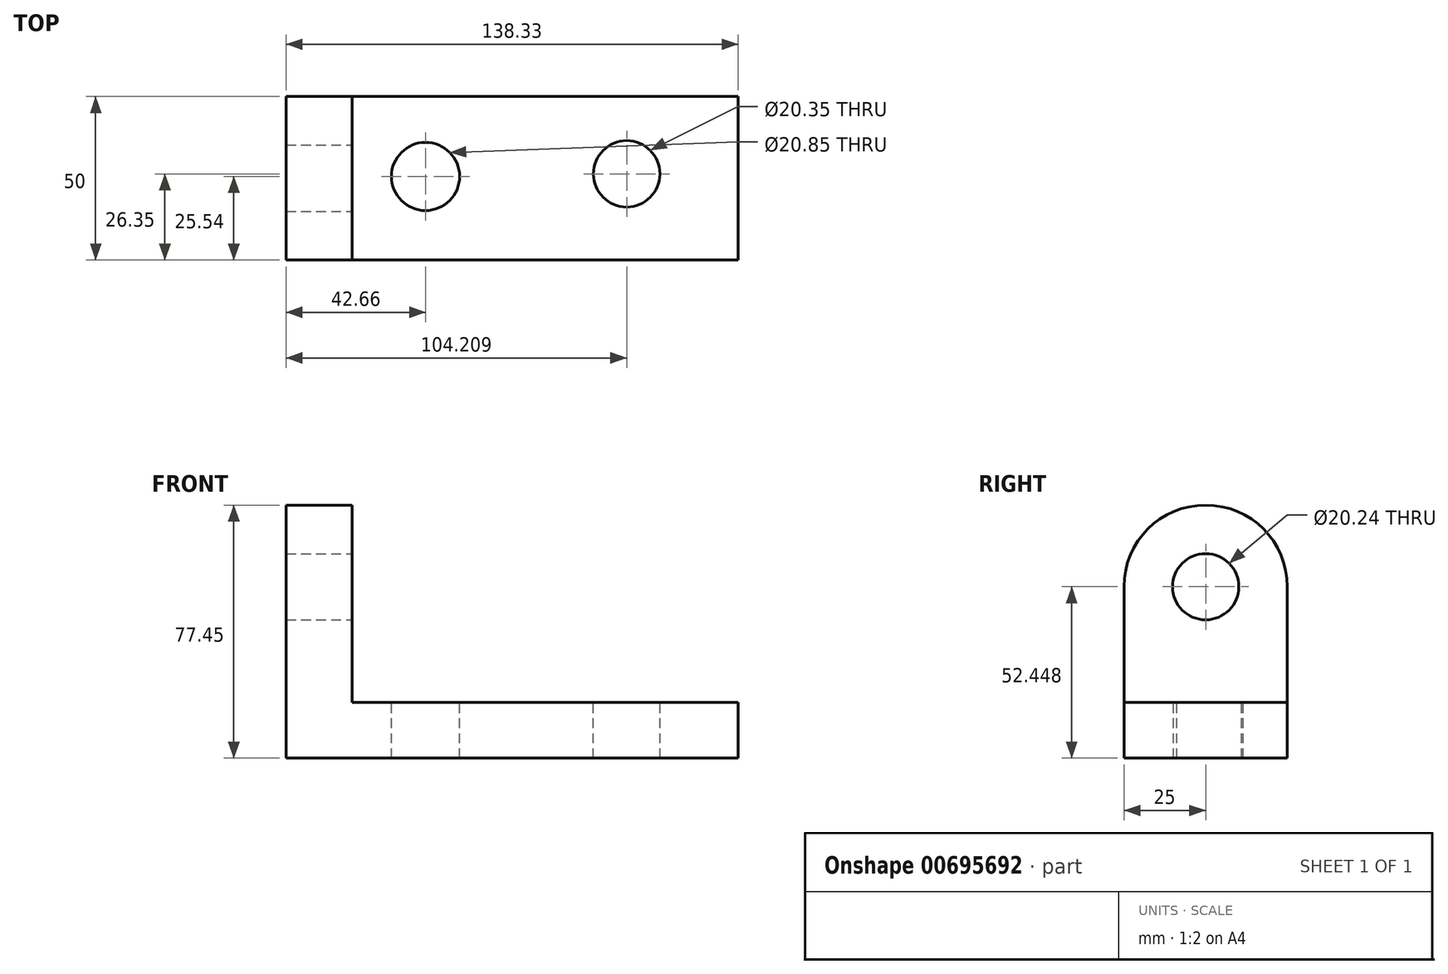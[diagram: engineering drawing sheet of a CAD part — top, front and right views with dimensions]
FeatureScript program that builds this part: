
annotation { "Feature Type Name" : "Feature", "Feature Type Description" : "" }
export const myFeature = defineFeature(function(context is Context, id is Id, definition is map)
    precondition{}
    {
        {
            var Q0;
            Q0=qCreatedBy(makeId("Front.planeOp"),FACE);
            var sketch = newSketch(context, id + "F0", { "sketchPlane" : qUnion([Q0])});
            skLineSegment(sketch, "E0", {"start": v(-87.52, -67.6) * mm, "end": v(50.8, -67.6) * mm});
            skLineSegment(sketch, "E1", {"start": v(50.8, -67.6) * mm, "end": v(50.8, -50.59) * mm});
            skLineSegment(sketch, "E2", {"start": v(50.8, -50.59) * mm, "end": v(-67.37, -50.59) * mm});
            skLineSegment(sketch, "E3", {"start": v(-67.37, -50.59) * mm, "end": v(-67.37, 9.85) * mm});
            skLineSegment(sketch, "E4", {"start": v(-67.37, 9.85) * mm, "end": v(-87.52, 9.85) * mm});
            skLineSegment(sketch, "E5", {"start": v(-87.52, 9.85) * mm, "end": v(-87.52, -67.6) * mm});
            skSolve(sketch);
        }
        {
            var Q0;
            Q0 = qSketchRegion(id + "F0", true);
            extrude(context, id + "F1", {"entities" : qUnion([Q0]), "depth" : 50 * mm, "offsetDistance" : 25 * mm});
        }
        {
            var Q0;
            Q0=makeQuery(id+"F1.opExtrude","CAP_EDGE",EDGE,{"disambiguationData":[OSD([sQuery(id+"F0.wireOp",EDGE,"E4")])],"isStart":false});
            var Q1;
            Q1=makeQuery(id+"F1.opExtrude","CAP_EDGE",EDGE,{"disambiguationData":[OSD([sQuery(id+"F0.wireOp",EDGE,"E4")])],"isStart":true});
            fillet(context, id + "F2", {"entities" : qUnion([Q0, Q1]), "radius" : 25 * mm, "tangentPropagation" : true, "allowEdgeOverflow" : false});
        }
        {
            var Q0;
            Q0=makeQuery(id+"F1.opExtrude","SWEPT_FACE",FACE,{"disambiguationData":[OSD([sQuery(id+"F0.wireOp",EDGE,"E2")])]});
            var sketch = newSketch(context, id + "F3", { "sketchPlane" : qUnion([Q0])});
            skCircle(sketch, "E6", {"center": v(-44.86, -24.46) * mm, "radius": 10.43 * mm});
            skCircle(sketch, "E7", {"center": v(16.69, -23.65) * mm, "radius": 10.18 * mm});
            skSolve(sketch);
        }
        {
            var Q0;
            Q0=makeQuery(id+"F3.imprint","IMPRINT",FACE,{"disambiguationData":[TD([[makeQuery(id+"F3.imprint","IMPRINT",EDGE,{"derivedFrom":sQuery(id+"F3.wireOp",EDGE,"E6")}),1.0]])]});
            var Q1;
            Q1=makeQuery(id+"F3.imprint","IMPRINT",FACE,{"disambiguationData":[TD([[makeQuery(id+"F3.imprint","IMPRINT",EDGE,{"derivedFrom":sQuery(id+"F3.wireOp",EDGE,"E7")}),1.0]])]});
            extrude(context, id + "F4", {"entities" : qUnion([Q0, Q1]), "operationType" : NewBodyOperationType.REMOVE, "oppositeDirection" : true, "depth" : 25 * mm, "offsetDistance" : 25 * mm});
        }
        {
            var Q0;
            Q0=makeQuery(id+"F1.opExtrude","SWEPT_FACE",FACE,{"disambiguationData":[OSD([sQuery(id+"F0.wireOp",EDGE,"E3")])]});
            var sketch = newSketch(context, id + "F5", { "sketchPlane" : qUnion([Q0])});
            skCircle(sketch, "E8", {"center": v(-25, -15.15) * mm, "radius": 10.12 * mm});
            skSolve(sketch);
        }
        {
            var Q0;
            Q0=makeQuery(id+"F5.imprint","IMPRINT",FACE,{"disambiguationData":[TD([[makeQuery(id+"F5.imprint","IMPRINT",EDGE,{"derivedFrom":sQuery(id+"F5.wireOp",EDGE,"E8")}),1.0]])]});
            extrude(context, id + "F6", {"entities" : qUnion([Q0]), "operationType" : NewBodyOperationType.REMOVE, "oppositeDirection" : true, "depth" : 25 * mm, "offsetDistance" : 25 * mm});
        }
    });
